# Revit family: Malvestio_332420
name_source: partatom
category: Furniture
revit_build: Autodesk Revit Architecture 2014 (Build: 20131024_2115(x64)
units: mm (PartAtom-declared; Revit-internal decimal feet)

## types (1)
- Malvestio_332420
    BIMobject category = Other Furniture
    Date of publishing = 2014-10-30
    Depth = 440 mm  [stored 1.44357 ft]
    Description = Bedside cabinet, double front, in plastic material, with the possibility to locate the overbed table on either side.
    Design country = Italy
    Edition number = 1
    Height = 750 mm  [stored 2.46063 ft]
    IFC Classification = Furniture
    Installation instructions = http://www.malvestio.it
    Manufacturer country = Italy
    Manufacturer name = Malvestio
    Manufacturer url = http://www.malvestio.it
    Material Main = Plastic-Malvestio-332420-Laminated
    Material Secondary = Stainless-Malvestio-332420-Steel
    Nominal height = 750
    Nominal width = 570
    Product SKU = ALL-WARDS-332420
    Product data url = http://www.malvestio.it
    QR code = http://malvestio.bimobject.com
    UNSPSC Code = 56
    UNSPSC Name = Furniture and Furnishings
    URL = http://malvestio.bimobject.com
    Weight Net (Kg) = 0
    Width = 570 mm  [stored 1.87008 ft]
    Youtube clip = http://www.malvestio.it

note: [stored X ft] marks values corroborated as IEEE doubles in the binary element streams (Revit-internal decimal feet)

## geometry (parser evidence)
native form markers: Sweep x3
no freeform markers — native parametric forms only
